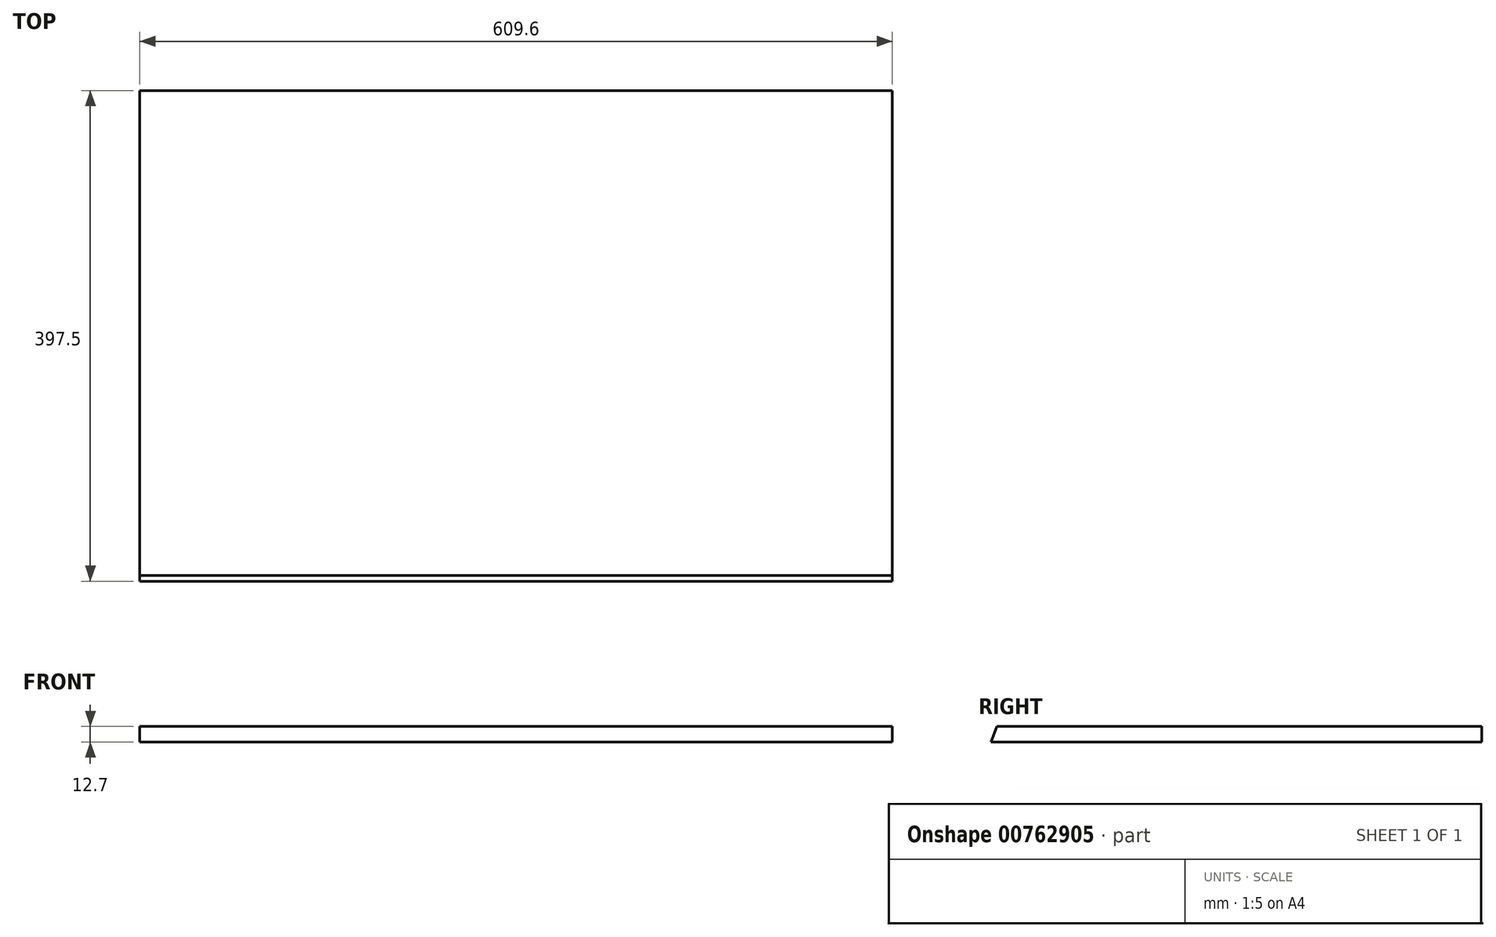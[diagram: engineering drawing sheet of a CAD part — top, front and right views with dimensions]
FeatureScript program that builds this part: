
annotation { "Feature Type Name" : "Feature", "Feature Type Description" : "" }
export const myFeature = defineFeature(function(context is Context, id is Id, definition is map)
    precondition{}
    {
        {
            var Q0;
            Q0=qCreatedBy(makeId("Right.planeOp"),FACE);
            var sketch = newSketch(context, id + "F0", { "sketchPlane" : qUnion([Q0])});
            skLineSegment(sketch, "E0", {"start": v(198.75, 0) * mm, "end": v(-198.75, 0) * mm});
            skLineSegment(sketch, "E1", {"start": v(-198.75, 0) * mm, "end": v(-194.13, 12.7) * mm});
            skLineSegment(sketch, "E2", {"start": v(-194.13, 12.7) * mm, "end": v(198.75, 12.7) * mm});
            skLineSegment(sketch, "E3", {"start": v(198.75, 12.7) * mm, "end": v(198.75, 0) * mm});
            skSolve(sketch);
        }
        {
            var Q0;
            Q0 = qSketchRegion(id + "F0", true);
            extrude(context, id + "F1", {"entities" : qUnion([Q0]), "depth" : 609.6 * mm, "offsetDistance" : 25.4 * mm, "symmetric" : true});
        }
    });
